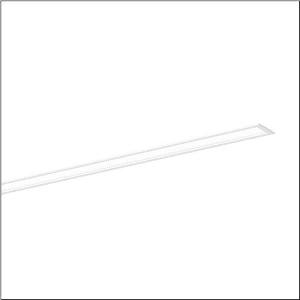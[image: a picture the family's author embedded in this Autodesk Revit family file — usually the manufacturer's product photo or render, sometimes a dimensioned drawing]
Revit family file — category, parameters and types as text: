
# Revit family: silica_r__21_51mx13dh31wb_20a9
name_source: partatom
category: Lighting Fixtures
units: mm (PartAtom-declared; Revit-internal decimal feet)

## family parameters
Cut with Voids When Loaded = No
Host = Face
Light Source = No
Part Type = Normal
Room Calculation Point = No
Round Connector Dimension = Use Diameter
Shared = No

## types (1)
- --- (1 x LED, 1640 lm, 13.8 W, 3000K)
    Apparent Load = 14 VA
    CIE Flux Codes = 78 96 99 100 100
    Color Rendering = 80
    Color Temperature = 3000K
    Default Elevation = 1800 mm
    Description = Silica® 21, office luminaire, primary optical cover: prismatic diffuser, of PMMA, CAT 2 (L<= 3000cd/m²), light emission: direct distribution, primary light characteristic: symmetric, installation type: recessed, LED, rated luminous flux: 1.640lm, luminous efficacy: 119lm/W, light colour: 830, colour temperature: 3000K, control gear: DALI 2, with terminal, 3+2-pole, max. 2.5mm², mains connection: 220..240V, AC, 50/60Hz, rated input power: 13.8W, luminaire housing, of aluminium, traffic white (RAL 9016), length: 628mm, width: 79mm, height: 53mm, protection rating (complete): IP20, insulation class (complete): insulation class I (protective earthing), certification: CE, permissible operating ambient temperature: 0..+35°C, standard: EN 50419, packaging unit: 1 piece
    Height = 0 mm  [stored 0 ft]
    Lamp = 1 x LED
    Lamp Light Flux = 1640 lm
    Lamp Power = 13.8 W
    Lamp count = 1
    Length = 627 mm
    Luminous efficacy = 119 lm/W
    Manufacturer = Siteco
    ModVariant = No
    Model = 51MX13DH31WB
    Mounting Place = Ceiling
    Mounting Type = Recessed
    Number of Poles = 1
    OnlyDefault = Yes
    Power Factor = 1
    Product Name = Silica® 21
    Product group = office luminaire | ceiling recessed
    ProductGroupID = 400
    Protection Class = Protection class I
    Protection Degree = IP 20
    RLX_Detail_Level = 1
    RLX_Emergency_Light_Flux = 0 lm
    RLX_Emergency_Type = 0
    RLX_Emergency_Type_DB = No
    RlxData = <blob elided: 14477 chars, md5=36c52702>
    Socket = socket
    Standby Power = 0 W
    System Light Flux = 1640 lm
    System Power = 14 W
    Type Comments = factory setting: luminous flux: 100 % | dim-lin: 254 | 170 mA
    Type Image = l_1335881.jpg
    URL = http://relux.com
    VarID = @adj_029151
    Voltage = 0 V
    Weight = 0.00 kg
    Width = 79 mm

note: [stored X ft] marks values corroborated as IEEE doubles in the binary element streams (Revit-internal decimal feet)

## geometry (parser evidence)
native form markers: Sweep x11
no freeform markers — native parametric forms only
